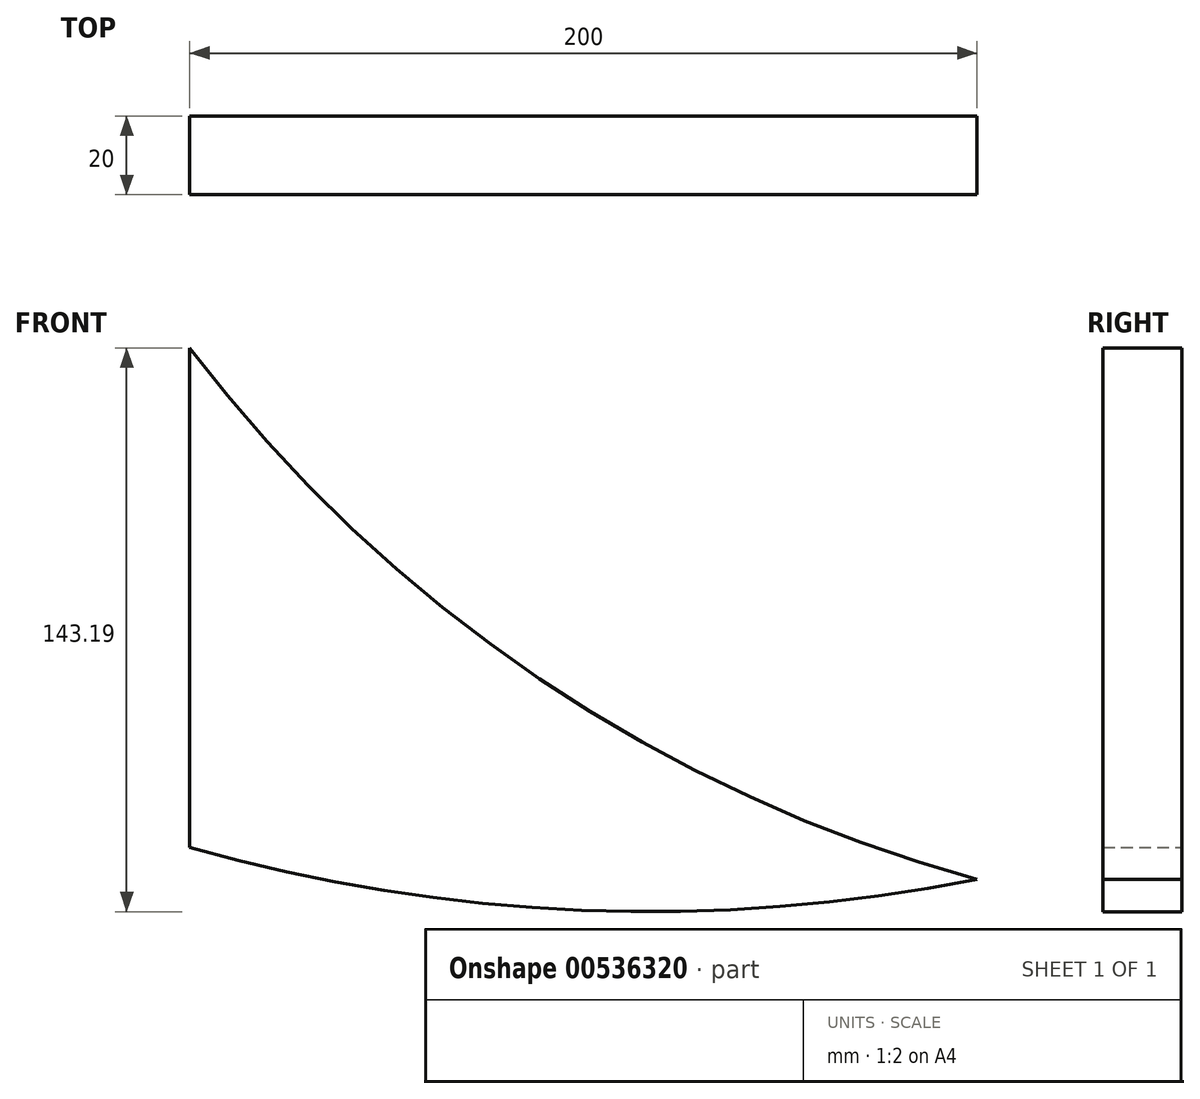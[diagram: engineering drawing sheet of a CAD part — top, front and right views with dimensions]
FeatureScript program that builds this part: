
annotation { "Feature Type Name" : "Feature", "Feature Type Description" : "" }
export const myFeature = defineFeature(function(context is Context, id is Id, definition is map)
    precondition{}
    {
        {
            var Q0;
            Q0=qCreatedBy(makeId("Front.planeOp"),FACE);
            var sketch = newSketch(context, id + "F0", { "sketchPlane" : qUnion([Q0])});
            skLineSegment(sketch, "E0", {"start": v(0, 0) * mm, "end": v(250, 0) * mm});
            skLineSegment(sketch, "E1.bottom", {"start": v(250, 0) * mm, "end": v(500, 0) * mm});
            skLineSegment(sketch, "E1.right", {"start": v(500, 0) * mm, "end": v(500, -500) * mm});
            skArc(sketch, "E2", {"start": v(250, 0) * mm, "mid": v(263.2, -305.9) * mm, "end": v(500, -500) * mm});
            skArc(sketch, "E3", {"start": v(0, 0) * mm, "mid": v(116.25, -383.75) * mm, "end": v(500, -500) * mm});
            skLineSegment(sketch, "E4", {"start": v(300, -365.04) * mm, "end": v(300, -491.87) * mm});
            skSolve(sketch);
        }
        {
            var Q0;
            {var subQ3=sQuery(id+"F0.wireOp",EDGE,"E4");Q0=makeQuery(id+"F0.imprint","IMPRINT",FACE,{"disambiguationData":[TD([[makeQuery(id+"F0.imprint","IMPRINT",EDGE,{"derivedFrom":subQ3}),1.0]])]});}
            extrude(context, id + "F1", {"entities" : qUnion([Q0]), "depth" : 20 * mm, "offsetDistance" : 25 * mm});
        }
    });
